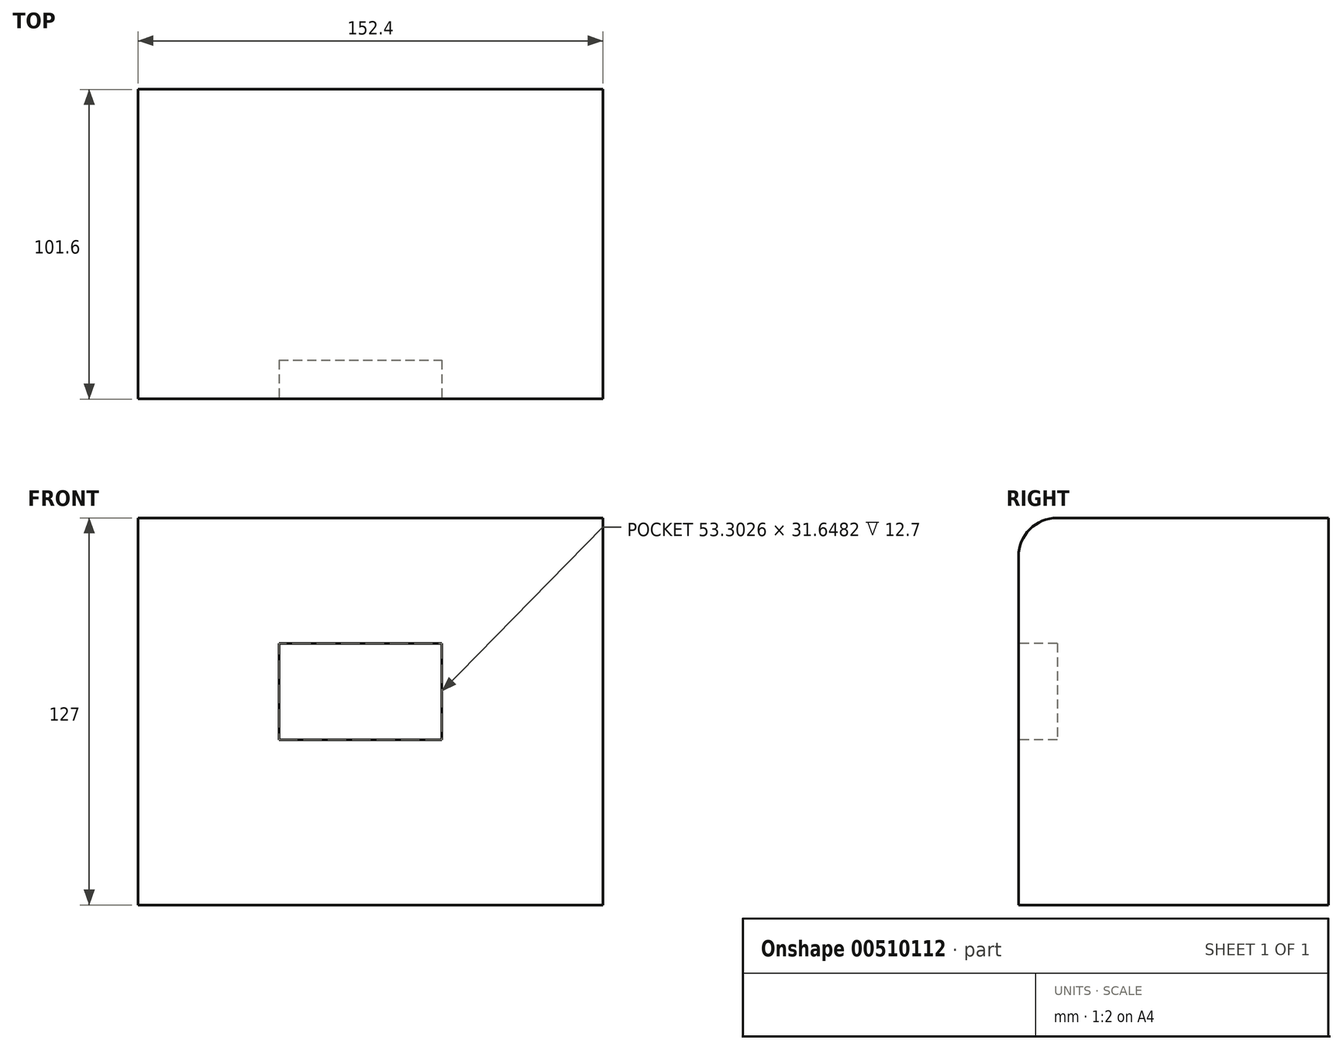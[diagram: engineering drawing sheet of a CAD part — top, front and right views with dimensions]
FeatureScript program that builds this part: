
annotation { "Feature Type Name" : "Feature", "Feature Type Description" : "" }
export const myFeature = defineFeature(function(context is Context, id is Id, definition is map)
    precondition{}
    {
        {
            var Q0;
            Q0=qCreatedBy(makeId("Top.planeOp"),FACE);
            var sketch = newSketch(context, id + "F0", { "sketchPlane" : qUnion([Q0])});
            skLineSegment(sketch, "E0.bottom", {"start": v(-62.08, 42.1) * mm, "end": v(90.32, 42.1) * mm});
            skLineSegment(sketch, "E0.top", {"start": v(-62.08, -59.5) * mm, "end": v(90.32, -59.5) * mm});
            skLineSegment(sketch, "E0.left", {"start": v(-62.08, 42.1) * mm, "end": v(-62.08, -59.5) * mm});
            skLineSegment(sketch, "E0.right", {"start": v(90.32, 42.1) * mm, "end": v(90.32, -59.5) * mm});
            skSolve(sketch);
        }
        {
            var Q0;
            Q0 = qSketchRegion(id + "F0", true);
            extrude(context, id + "F1", {"entities" : qUnion([Q0]), "depth" : 127 * mm});
        }
        {
            var Q0;
            Q0=makeQuery(id+"F1.opExtrude","CAP_EDGE",EDGE,{"disambiguationData":[OSD([sQuery(id+"F0.wireOp",EDGE,"E0.top")])],"isStart":false});
            fillet(context, id + "F2", {"entities" : qUnion([Q0]), "radius" : 12.7 * mm, "tangentPropagation" : true, "allowEdgeOverflow" : false});
        }
        {
            var Q0;
            Q0=makeQuery(id+"F1.opExtrude","SWEPT_FACE",FACE,{"disambiguationData":[OSD([sQuery(id+"F0.wireOp",EDGE,"E0.top")])]});
            var sketch = newSketch(context, id + "F3", { "sketchPlane" : qUnion([Q0])});
            skLineSegment(sketch, "E1.bottom", {"start": v(-15.8, 85.84) * mm, "end": v(37.5, 85.84) * mm});
            skLineSegment(sketch, "E1.top", {"start": v(-15.8, 54.2) * mm, "end": v(37.5, 54.2) * mm});
            skLineSegment(sketch, "E1.left", {"start": v(-15.8, 85.84) * mm, "end": v(-15.8, 54.2) * mm});
            skLineSegment(sketch, "E1.right", {"start": v(37.5, 85.84) * mm, "end": v(37.5, 54.2) * mm});
            skSolve(sketch);
        }
        {
            var Q0;
            Q0=makeQuery(id+"F3.imprint","IMPRINT",FACE,{"disambiguationData":[TD([[makeQuery(id+"F3.imprint","IMPRINT",EDGE,{"derivedFrom":sQuery(id+"F3.wireOp",EDGE,"E1.bottom")}),-1.0]])]});
            extrude(context, id + "F4", {"entities" : qUnion([Q0]), "operationType" : NewBodyOperationType.REMOVE, "oppositeDirection" : true, "depth" : 12.7 * mm});
        }
    });
